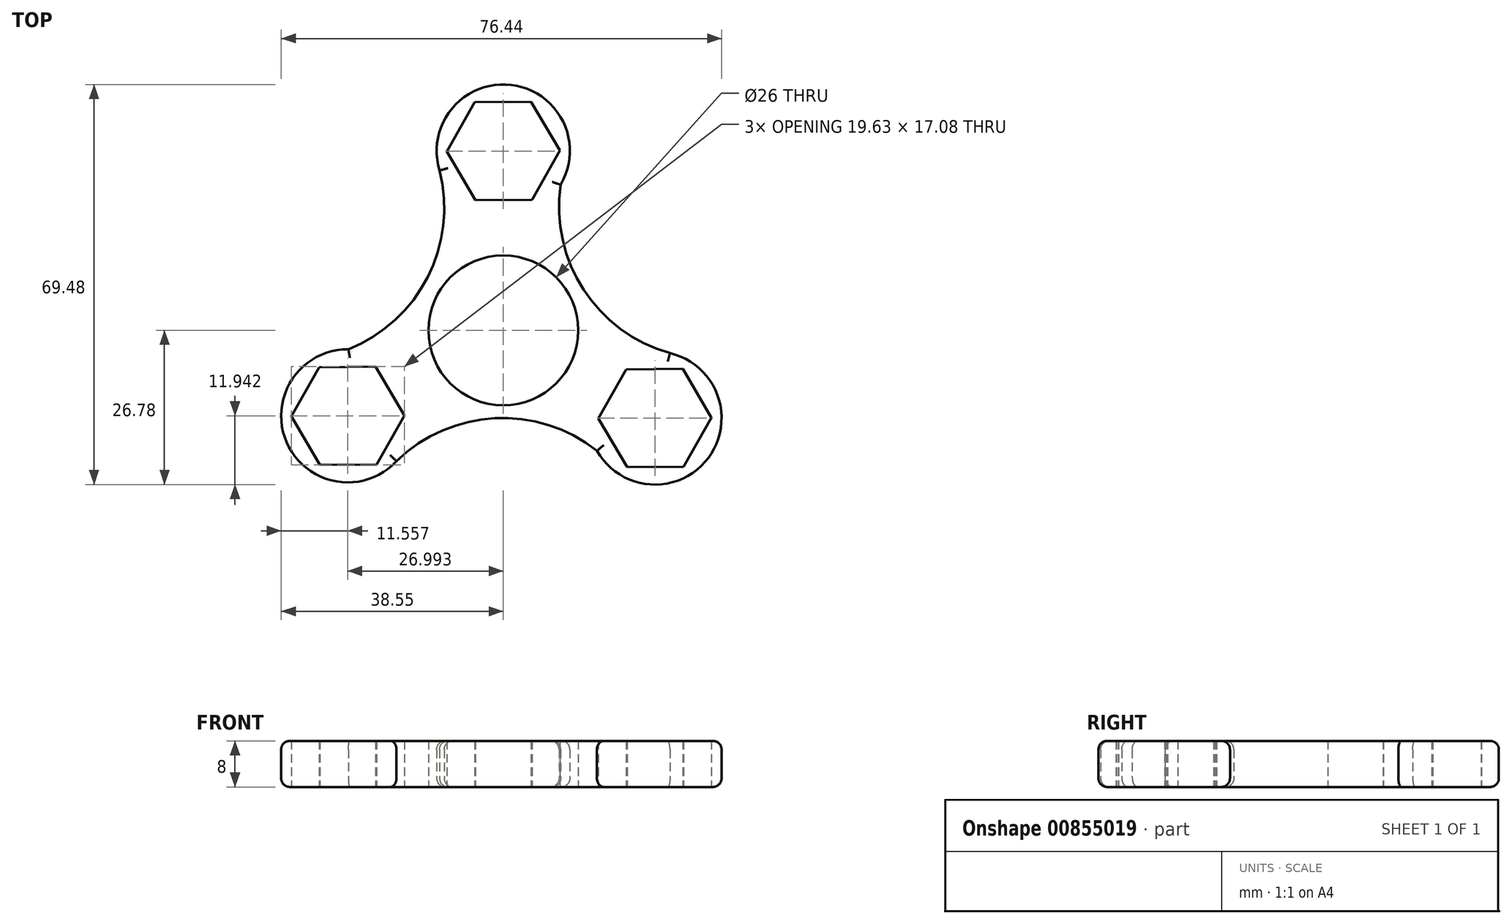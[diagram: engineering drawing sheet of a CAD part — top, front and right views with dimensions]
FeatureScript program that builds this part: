
annotation { "Feature Type Name" : "Feature", "Feature Type Description" : "" }
export const myFeature = defineFeature(function(context is Context, id is Id, definition is map)
    precondition{}
    {
        {
            var Q0;
            Q0=qCreatedBy(makeId("Top.planeOp"),FACE);
            var sketch = newSketch(context, id + "F0", { "sketchPlane" : qUnion([Q0])});
            skCircle(sketch, "E0", {"center": v(0, 0) * mm, "radius": 13 * mm});
            skArc(sketch, "E1.cCircle", {"start": v(-7.4, 35.33) * mm, "mid": v(-8.5, 31.08) * mm, "end": v(-7.33, 26.83) * mm, "construction": true});
            skLineSegment(sketch, "E1.0", {"start": v(-4.84, 22.6) * mm, "end": v(-9.81, 31.06) * mm});
            skLineSegment(sketch, "E1.1", {"start": v(-9.81, 31.06) * mm, "end": v(-4.98, 39.6) * mm});
            skLineSegment(sketch, "E1.2", {"start": v(-4.98, 39.6) * mm, "end": v(4.84, 39.68) * mm});
            skLineSegment(sketch, "E1.3", {"start": v(4.84, 39.68) * mm, "end": v(9.81, 31.22) * mm});
            skLineSegment(sketch, "E1.4", {"start": v(9.81, 31.22) * mm, "end": v(4.98, 22.68) * mm});
            skLineSegment(sketch, "E1.5", {"start": v(4.98, 22.68) * mm, "end": v(-4.84, 22.6) * mm});
            skPoint(sketch, "E1.0.midPoint", {"position": v(-7.33, 26.83) * mm});
            skArc(sketch, "E2", {"start": v(9.96, 25.28) * mm, "mid": v(1.36, 42.62) * mm, "end": v(-11.05, 27.76) * mm});
            skArc(sketch, "E3.1.0", {"start": v(-26.9, -3.28) * mm, "mid": v(-37.61, -19.4) * mm, "end": v(-18.54, -22.72) * mm});
            skLineSegment(sketch, "E3.1.1", {"start": v(-22.15, -6.3) * mm, "end": v(-17.18, -14.76) * mm});
            skLineSegment(sketch, "E3.1.2", {"start": v(-17.18, -14.76) * mm, "end": v(-22.02, -23.3) * mm});
            skLineSegment(sketch, "E3.1.3", {"start": v(-22.02, -23.3) * mm, "end": v(-31.83, -23.38) * mm});
            skLineSegment(sketch, "E3.1.4", {"start": v(-31.83, -23.38) * mm, "end": v(-36.8, -14.92) * mm});
            skLineSegment(sketch, "E3.1.5", {"start": v(-36.8, -14.92) * mm, "end": v(-31.97, -6.38) * mm});
            skLineSegment(sketch, "E3.1.6", {"start": v(-31.97, -6.38) * mm, "end": v(-22.15, -6.3) * mm});
            skArc(sketch, "E3.2.0", {"start": v(16.26, -20.92) * mm, "mid": v(35.59, -22.14) * mm, "end": v(28.92, -3.96) * mm});
            skLineSegment(sketch, "E3.2.1", {"start": v(16.51, -15.3) * mm, "end": v(21.35, -6.76) * mm});
            skLineSegment(sketch, "E3.2.2", {"start": v(21.35, -6.76) * mm, "end": v(31.16, -6.68) * mm});
            skLineSegment(sketch, "E3.2.3", {"start": v(31.16, -6.68) * mm, "end": v(36.14, -15.14) * mm});
            skLineSegment(sketch, "E3.2.4", {"start": v(36.14, -15.14) * mm, "end": v(31.3, -23.68) * mm});
            skLineSegment(sketch, "E3.2.5", {"start": v(31.3, -23.68) * mm, "end": v(21.49, -23.76) * mm});
            skLineSegment(sketch, "E3.2.6", {"start": v(21.49, -23.76) * mm, "end": v(16.51, -15.3) * mm});
            skPoint(sketch, "E3.center", {"position": v(-0.22, 0.36) * mm});
            skArc(sketch, "E4", {"start": v(11.56, 31.22) * mm, "mid": v(12.4, 9.76) * mm, "end": v(28.92, -3.96) * mm});
            skArc(sketch, "E5.1.0", {"start": v(-32.84, -4.87) * mm, "mid": v(-14.68, 6.6) * mm, "end": v(-11.05, 27.76) * mm});
            skArc(sketch, "E5.2.0", {"start": v(20.62, -25.27) * mm, "mid": v(1.6, -15.28) * mm, "end": v(-18.54, -22.72) * mm});
            skLineSegment(sketch, "E6.trimOffspring", {"start": v(11.26, 6.5) * mm, "end": v(13.49, 7.79) * mm, "construction": true});
            skLineSegment(sketch, "E7.trimOffspring", {"start": v(11.94, 10.75) * mm, "end": v(14.75, 5.9) * mm, "construction": true});
            skLineSegment(sketch, "E8.trimOffspring", {"start": v(21.01, -4.96) * mm, "end": v(22.05, -6.76) * mm, "construction": true});
            skSolve(sketch);
        }
        {
            var Q0;
            Q0=qSketchRegion(id+"F0",true);
            extrude(context, id + "F1", {"entities" : qUnion([Q0]), "depth" : 8 * mm, "offsetDistance" : 25 * mm});
        }
        {
            var Q0;
            Q0=makeQuery(id+"F1.opExtrude","CAP_EDGE",EDGE,{"disambiguationData":[OSD([sQuery(id+"F0.wireOp",EDGE,"E5.2.0")])],"isStart":false});
            var Q1;
            Q1=makeQuery(id+"F1.opExtrude","CAP_EDGE",EDGE,{"disambiguationData":[OSD([sQuery(id+"F0.wireOp",EDGE,"E3.1.0")])],"isStart":false});
            var Q2;
            Q2=makeQuery(id+"F1.opExtrude","CAP_EDGE",EDGE,{"disambiguationData":[OSD([sQuery(id+"F0.wireOp",EDGE,"E5.1.0")])],"isStart":false});
            var Q3;
            Q3=makeQuery(id+"F1.opExtrude","CAP_EDGE",EDGE,{"disambiguationData":[OSD([sQuery(id+"F0.wireOp",EDGE,"E2")])],"isStart":false});
            var Q4;
            Q4=makeQuery(id+"F1.opExtrude","CAP_EDGE",EDGE,{"disambiguationData":[OSD([sQuery(id+"F0.wireOp",EDGE,"E3.2.0")])],"isStart":false});
            var Q5;
            Q5=makeQuery(id+"F1.opExtrude","CAP_EDGE",EDGE,{"disambiguationData":[OSD([sQuery(id+"F0.wireOp",EDGE,"E4")])],"isStart":false});
            fillet(context, id + "F2", {"entities" : qUnion([Q0, Q1, Q2, Q3, Q4, Q5]), "radius" : 1.5 * mm, "tangentPropagation" : true, "allowEdgeOverflow" : false});
        }
        {
            var Q0;
            Q0=makeQuery(id+"F1.opExtrude","CAP_EDGE",EDGE,{"disambiguationData":[OSD([sQuery(id+"F0.wireOp",EDGE,"E3.1.0")])],"isStart":true});
            var Q1;
            Q1=makeQuery(id+"F1.opExtrude","CAP_EDGE",EDGE,{"disambiguationData":[OSD([sQuery(id+"F0.wireOp",EDGE,"E5.2.0")])],"isStart":true});
            var Q2;
            Q2=makeQuery(id+"F1.opExtrude","CAP_EDGE",EDGE,{"disambiguationData":[OSD([sQuery(id+"F0.wireOp",EDGE,"E3.2.0")])],"isStart":true});
            var Q3;
            Q3=makeQuery(id+"F1.opExtrude","CAP_EDGE",EDGE,{"disambiguationData":[OSD([sQuery(id+"F0.wireOp",EDGE,"E4")])],"isStart":true});
            var Q4;
            Q4=makeQuery(id+"F1.opExtrude","CAP_EDGE",EDGE,{"disambiguationData":[OSD([sQuery(id+"F0.wireOp",EDGE,"E2")])],"isStart":true});
            var Q5;
            Q5=makeQuery(id+"F1.opExtrude","CAP_EDGE",EDGE,{"disambiguationData":[OSD([sQuery(id+"F0.wireOp",EDGE,"E5.1.0")])],"isStart":true});
            fillet(context, id + "F3", {"entities" : qUnion([Q0, Q1, Q2, Q3, Q4, Q5]), "radius" : 1.5 * mm, "tangentPropagation" : true, "allowEdgeOverflow" : false});
        }
    });
